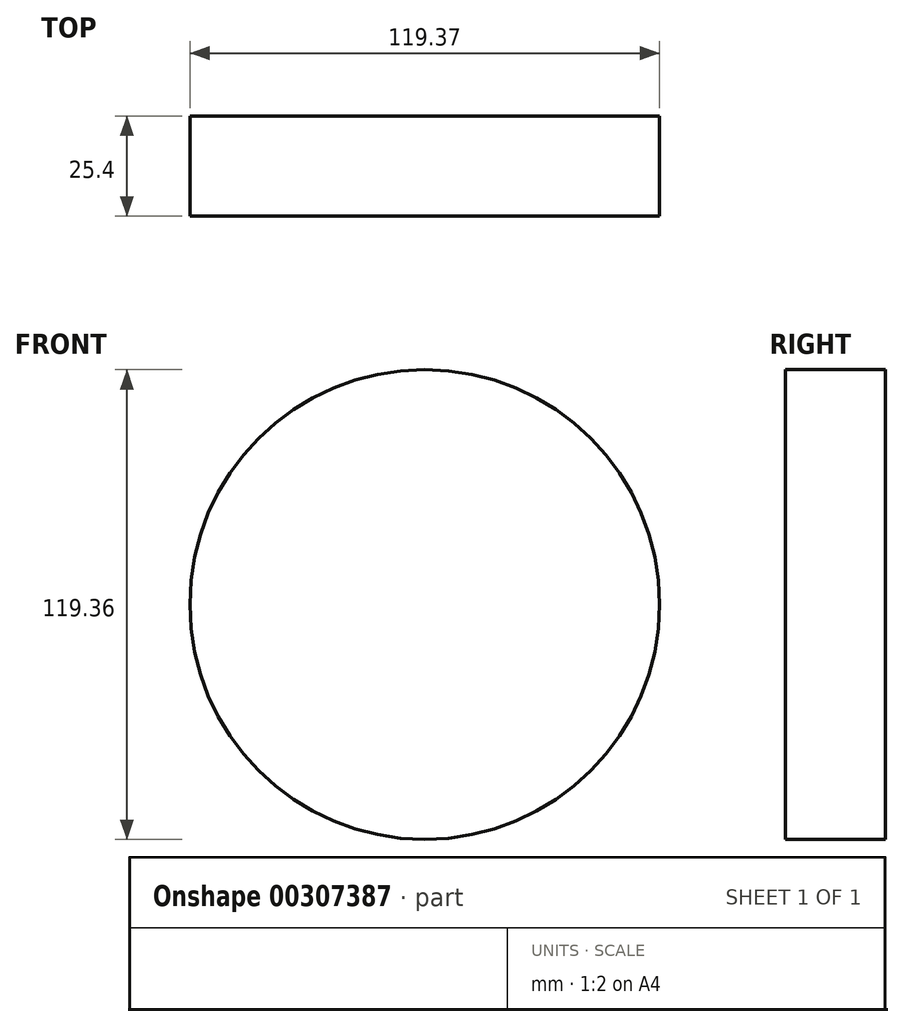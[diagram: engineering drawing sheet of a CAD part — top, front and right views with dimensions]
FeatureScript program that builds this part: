
annotation { "Feature Type Name" : "Feature", "Feature Type Description" : "" }
export const myFeature = defineFeature(function(context is Context, id is Id, definition is map)
    precondition{}
    {
        {
            var Q0;
            Q0=qCreatedBy(makeId("Front.planeOp"),FACE);
            var sketch = newSketch(context, id + "F0", { "sketchPlane" : qUnion([Q0])});
            skCircle(sketch, "E0", {"center": v(2.66, 0) * mm, "radius": 59.68 * mm});
            skSolve(sketch);
        }
        {
            var Q0;
            Q0=makeQuery(id+"F0.imprint","IMPRINT",FACE,{"disambiguationData":[TD([[makeQuery(id+"F0.imprint","IMPRINT",EDGE,{"derivedFrom":sQuery(id+"F0.wireOp",EDGE,"E0")}),1.0]])]});
            extrude(context, id + "F1", {"entities" : qUnion([Q0]), "depth" : 25.4 * mm});
        }
    });
